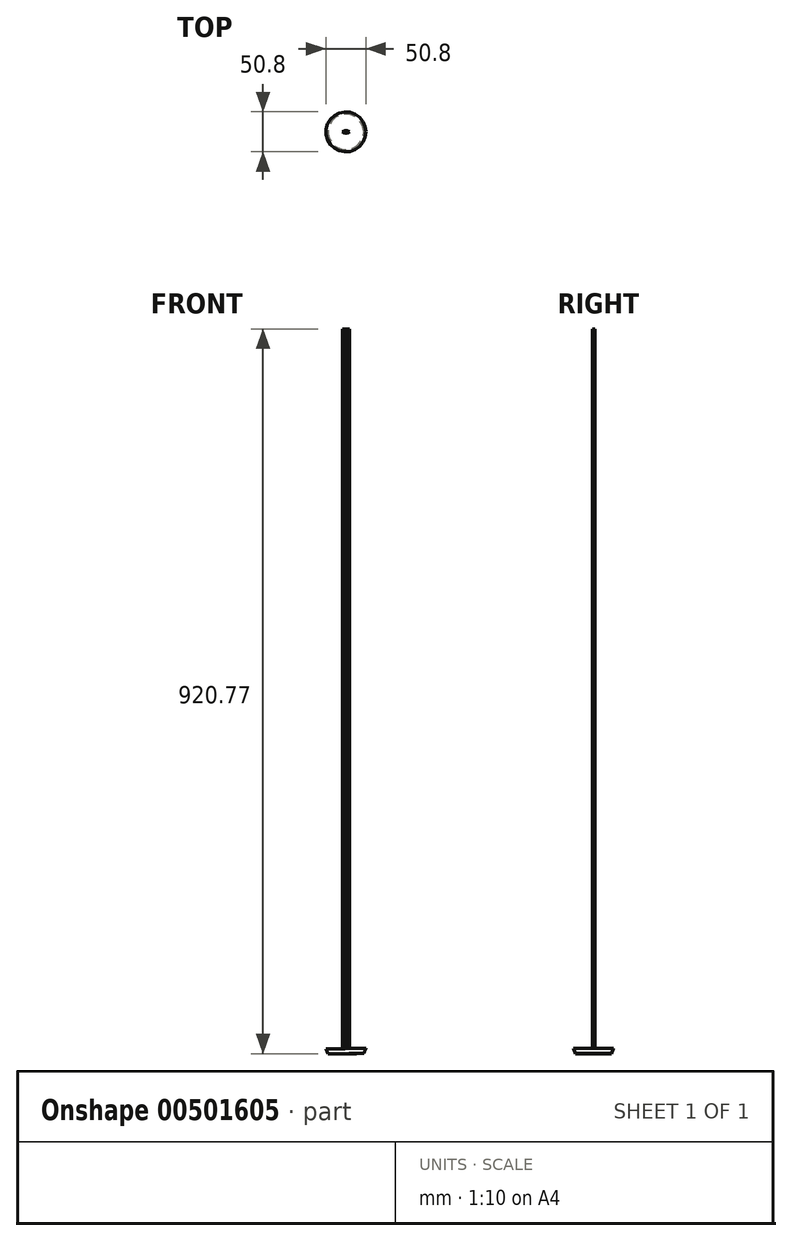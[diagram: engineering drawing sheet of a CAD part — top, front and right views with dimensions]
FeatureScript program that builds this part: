
annotation { "Feature Type Name" : "Feature", "Feature Type Description" : "" }
export const myFeature = defineFeature(function(context is Context, id is Id, definition is map)
    precondition{}
    {
        {
            var Q0;
            Q0=qCreatedBy(makeId("Front.planeOp"),FACE);
            var sketch = newSketch(context, id + "F0", { "sketchPlane" : qUnion([Q0])});
            skLineSegment(sketch, "E0.bottom", {"start": v(-24.03, -22.65) * mm, "end": v(-11.33, -22.65) * mm});
            skLineSegment(sketch, "E0.top", {"start": v(-24.03, 891.75) * mm, "end": v(-11.33, 891.75) * mm});
            skLineSegment(sketch, "E0.left", {"start": v(-24.03, -22.65) * mm, "end": v(-24.03, 891.75) * mm});
            skLineSegment(sketch, "E0.right", {"start": v(-11.33, -22.65) * mm, "end": v(-11.33, 891.75) * mm});
            skLineSegment(sketch, "E1", {"start": v(-17.68, 891.75) * mm, "end": v(-17.68, -22.65) * mm});
            skLineSegment(sketch, "E2", {"start": v(-17.68, -22.65) * mm, "end": v(-43.08, -22.65) * mm});
            skLineSegment(sketch, "E3.MirrorCS", {"start": v(-17.68, -22.65) * mm, "end": v(-11.33, -22.65) * mm});
            skLineSegment(sketch, "E4.bottom", {"start": v(-43.08, -22.65) * mm, "end": v(-11.33, -22.65) * mm});
            skLineSegment(sketch, "E4.left", {"start": v(-43.08, -22.65) * mm, "end": v(-40.4, -29.02) * mm});
            skPoint(sketch, "E5", {"position": v(-17.64, -29.02) * mm});
            skLineSegment(sketch, "E6", {"start": v(-40.4, -29.02) * mm, "end": v(-17.64, -29.02) * mm});
            skPoint(sketch, "E7", {"position": v(-29.01, -29.02) * mm});
            skLineSegment(sketch, "E8.bottom", {"start": v(-29.01, -29.02) * mm, "end": v(-17.64, -29.02) * mm});
            skLineSegment(sketch, "E8.top", {"start": v(-29.01, -276.64) * mm, "end": v(-16.07, -276.64) * mm});
            skLineSegment(sketch, "E8.left", {"start": v(-29.01, -29.02) * mm, "end": v(-29.01, -276.64) * mm});
            skPoint(sketch, "E9", {"position": v(-16.07, -276.64) * mm});
            skLineSegment(sketch, "E10", {"start": v(-17.68, -22.65) * mm, "end": v(-16.07, -276.64) * mm});
            skSolve(sketch);
        }
        {
            var Q0;
            {var subQ0=sQuery(id+"F0.wireOp",EDGE,"E8.bottom");Q0=makeQuery(id+"F0.imprint","IMPRINT",FACE,{"disambiguationData":[TD([[makeQuery(id+"F0.imprint","IMPRINT",EDGE,{"derivedFrom":subQ0}),-1.0]])]});}
            var Q1;
            {var subQ0=sQuery(id+"F0.wireOp",EDGE,"E4.left");Q1=makeQuery(id+"F0.imprint","IMPRINT",FACE,{"disambiguationData":[TD([[makeQuery(id+"F0.imprint","IMPRINT",EDGE,{"derivedFrom":subQ0}),1.0]])]});}
            var Q2;
            Q2=sQuery(id+"F0.wireOp",EDGE,"E10");
            revolve(context, id + "F1", {"entities" : qUnion([Q0, Q1]), "axis" : qUnion([Q2]), "revolveType" : RevolveType.FULL});
        }
        {
            var Q0;
            {var subQ0=sQuery(id+"F0.wireOp",EDGE,"E0.right");Q0=makeQuery(id+"F0.imprint","IMPRINT",FACE,{"disambiguationData":[TD([[makeQuery(id+"F0.imprint","IMPRINT",EDGE,{"derivedFrom":subQ0}),1.0]])]});}
            var Q1;
            {var subQ0=sQuery(id+"F0.wireOp",EDGE,"E0.left");Q1=makeQuery(id+"F0.imprint","IMPRINT",FACE,{"disambiguationData":[TD([[makeQuery(id+"F0.imprint","IMPRINT",EDGE,{"derivedFrom":subQ0}),-1.0]])]});}
            extrude(context, id + "F2", {"entities" : qUnion([Q0, Q1]), "operationType" : NewBodyOperationType.ADD, "depth" : 1.59 * mm});
        }
        {
            var Q0;
            {var subQ0=sQuery(id+"F0.wireOp",EDGE,"E0.right");Q0=makeQuery(id+"F0.imprint","IMPRINT",FACE,{"disambiguationData":[TD([[makeQuery(id+"F0.imprint","IMPRINT",EDGE,{"derivedFrom":subQ0}),1.0]])]});}
            var Q1;
            {var subQ0=sQuery(id+"F0.wireOp",EDGE,"E0.left");Q1=makeQuery(id+"F0.imprint","IMPRINT",FACE,{"disambiguationData":[TD([[makeQuery(id+"F0.imprint","IMPRINT",EDGE,{"derivedFrom":subQ0}),-1.0]])]});}
            extrude(context, id + "F3", {"entities" : qUnion([Q0, Q1]), "operationType" : NewBodyOperationType.ADD, "oppositeDirection" : true, "depth" : 1.59 * mm});
        }
        {
            var Q0;
            Q0=makeQuery(id+"F3.opExtrude","CAP_EDGE",EDGE,{"disambiguationData":[OSD([sQuery(id+"F0.wireOp",EDGE,"E0.right")])],"isStart":false});
            var Q1;
            Q1=makeQuery(id+"F2.opExtrude","CAP_EDGE",EDGE,{"disambiguationData":[OSD([sQuery(id+"F0.wireOp",EDGE,"E0.right")])],"isStart":false});
            var Q2;
            Q2=makeQuery(id+"F2.opExtrude","CAP_EDGE",EDGE,{"disambiguationData":[OSD([sQuery(id+"F0.wireOp",EDGE,"E0.left")])],"isStart":false});
            var Q3;
            Q3=makeQuery(id+"F3.opExtrude","CAP_EDGE",EDGE,{"disambiguationData":[OSD([sQuery(id+"F0.wireOp",EDGE,"E0.left")])],"isStart":false});
            chamfer(context, id + "F4", {"entities" : qUnion([Q0, Q1, Q2, Q3]), "chamferType" : ChamferType.TWO_OFFSETS, "width1" : 2.54 * mm, "oppositeDirection" : false, "width2" : 5.08 * mm, "tangentPropagation" : true});
        }
    });
